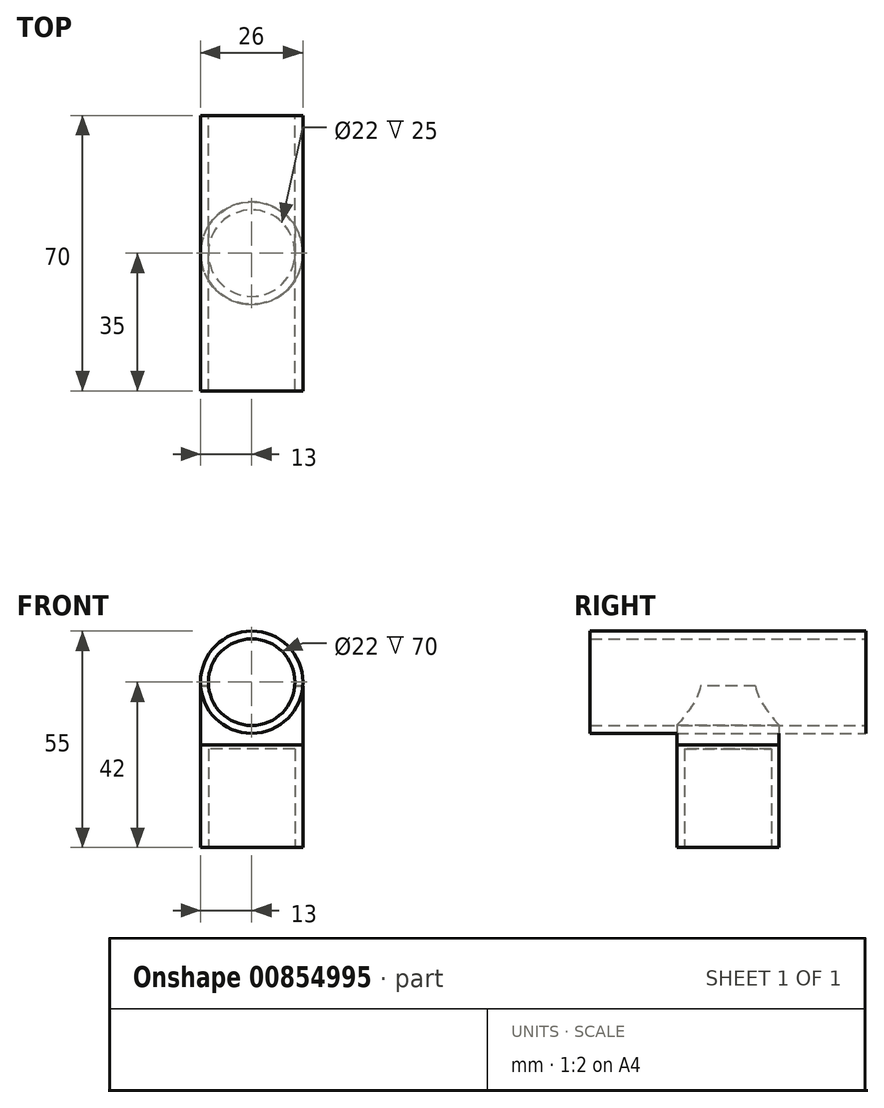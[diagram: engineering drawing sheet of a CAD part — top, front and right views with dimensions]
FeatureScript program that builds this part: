
annotation { "Feature Type Name" : "Feature", "Feature Type Description" : "" }
export const myFeature = defineFeature(function(context is Context, id is Id, definition is map)
    precondition{}
    {
        {
            var Q0;
            Q0=qCreatedBy(makeId("Top.planeOp"),FACE);
            var sketch = newSketch(context, id + "F0", { "sketchPlane" : qUnion([Q0])});
            skCircle(sketch, "E0", {"center": v(0, 0) * mm, "radius": 11 * mm});
            skCircle(sketch, "E1", {"center": v(0, 0) * mm, "radius": 13 * mm});
            skSolve(sketch);
        }
        {
            var Q0;
            Q0=makeQuery(id+"F0.imprint","IMPRINT",FACE,{"disambiguationData":[TD([[makeQuery(id+"F0.imprint","IMPRINT",EDGE,{"derivedFrom":sQuery(id+"F0.wireOp",EDGE,"E0")}),-1.0]])]});
            extrude(context, id + "F1", {"entities" : qUnion([Q0]), "depth" : 25 * mm, "offsetDistance" : 25 * mm});
        }
        {
            var Q0;
            Q0=qCreatedBy(makeId("Front.planeOp"),FACE);
            var sketch = newSketch(context, id + "F2", { "sketchPlane" : qUnion([Q0])});
            skCircle(sketch, "E2", {"center": v(0, 42) * mm, "radius": 11 * mm});
            skCircle(sketch, "E3", {"center": v(0, 42) * mm, "radius": 13 * mm});
            skSolve(sketch);
        }
        {
            var Q0;
            Q0 = qSketchRegion(id + "F2", true);
            extrude(context, id + "F3", {"entities" : qUnion([Q0]), "endBound" : BoundingType.SYMMETRIC, "depth" : 70 * mm, "offsetDistance" : 25 * mm});
        }
        {
            var Q0;
            Q0=makeQuery(id+"F1.opExtrude","CAP_FACE",FACE,{"disambiguationData":[OSD([sQuery(id+"F0.wireOp",EDGE,"E0"),sQuery(id+"F0.wireOp",EDGE,"E1")])],"isStart":false});
            var sketch = newSketch(context, id + "F4", { "sketchPlane" : qUnion([Q0])});
            skCircle(sketch, "E4", {"center": v(0, 0) * mm, "radius": 13 * mm});
            skSolve(sketch);
        }
        {
            var Q0;
            Q0 = qSketchRegion(id + "F4", true);
            extrude(context, id + "F5", {"entities" : qUnion([Q0]), "operationType" : NewBodyOperationType.ADD, "depth" : 1 * mm, "offsetDistance" : 25 * mm});
        }
        {
            var Q0;
            Q0=makeQuery(id+"F5.opExtrude","CAP_FACE",FACE,{"disambiguationData":[OSD([sQuery(id+"F4.wireOp",EDGE,"E4")])],"isStart":false});
            var sketch = newSketch(context, id + "F6", { "sketchPlane" : qUnion([Q0])});
            skCircle(sketch, "E5", {"center": v(0, 0) * mm, "radius": 13 * mm});
            skSolve(sketch);
        }
        {
            var Q0;
            Q0 = qSketchRegion(id + "F6", true);
            extrude(context, id + "F7", {"entities" : qUnion([Q0]), "depth" : 15 * mm, "offsetDistance" : 25 * mm});
        }
        {
            var Q0;
            Q0=makeQuery(id+"F3.opExtrude","CAP_FACE",FACE,{"disambiguationData":[OSD([sQuery(id+"F2.wireOp",EDGE,"E2"),sQuery(id+"F2.wireOp",EDGE,"E3")])],"isStart":false});
            var sketch = newSketch(context, id + "F8", { "sketchPlane" : qUnion([Q0])});
            skCircle(sketch, "E6", {"center": v(0, 42) * mm, "radius": 11 * mm});
            skSolve(sketch);
        }
        {
            var Q0;
            Q0 = qSketchRegion(id + "F8", true);
            extrude(context, id + "F9", {"entities" : qUnion([Q0]), "operationType" : NewBodyOperationType.REMOVE, "oppositeDirection" : true, "depth" : 70 * mm, "offsetDistance" : 25 * mm});
        }
    });
